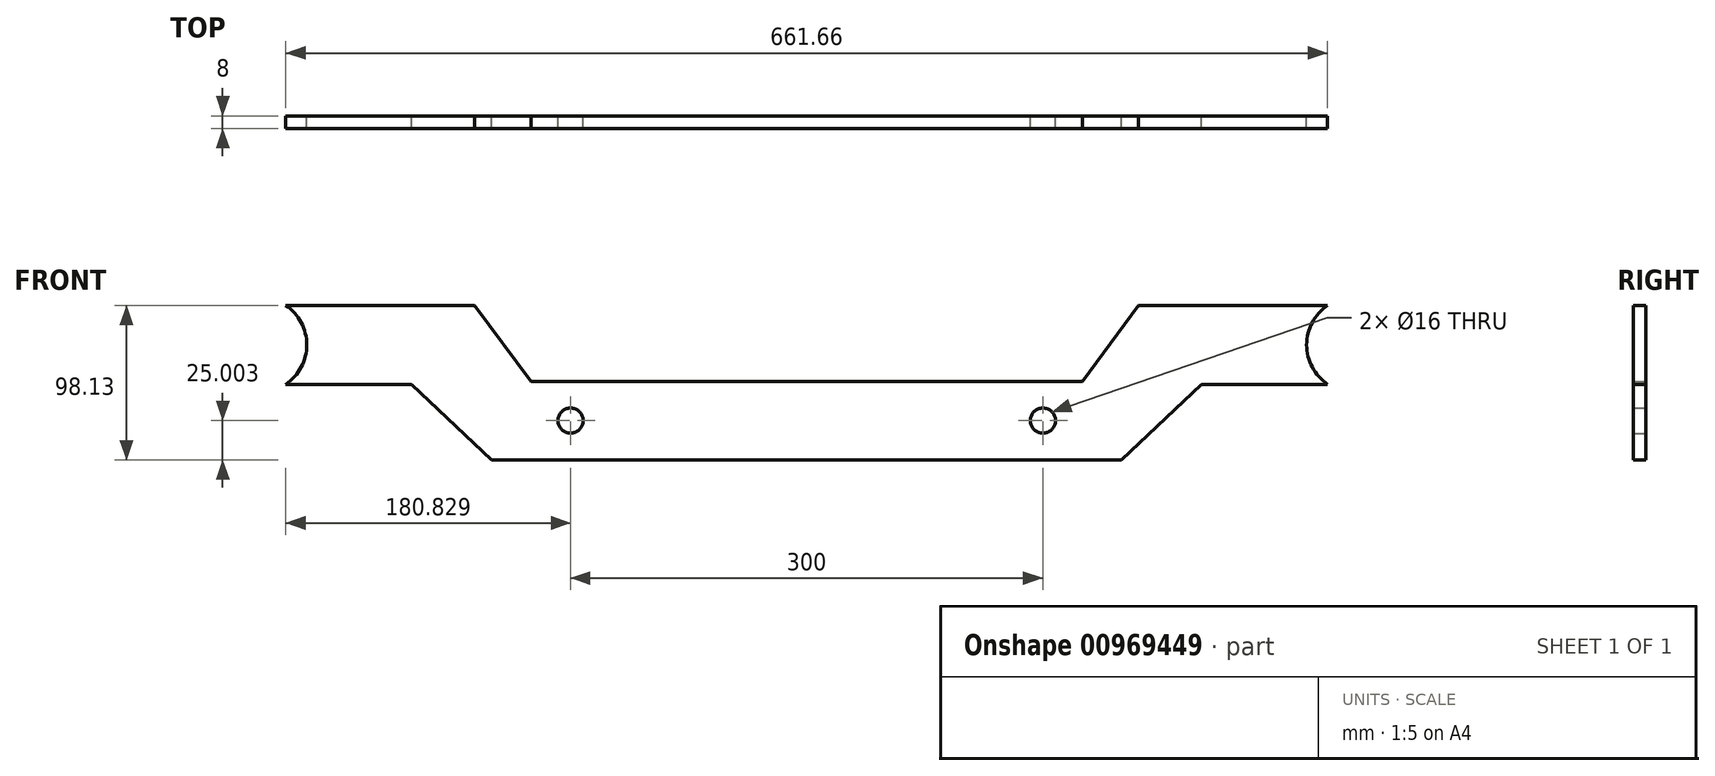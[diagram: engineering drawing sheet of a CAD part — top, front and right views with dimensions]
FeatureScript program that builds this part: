
annotation { "Feature Type Name" : "Feature", "Feature Type Description" : "" }
export const myFeature = defineFeature(function(context is Context, id is Id, definition is map)
    precondition{}
    {
        {
            var Q0;
            Q0=qCreatedBy(makeId("Front.planeOp"),FACE);
            var sketch = newSketch(context, id + "F0", { "sketchPlane" : qUnion([Q0])});
            skLineSegment(sketch, "E0", {"start": v(-200.2, -56.86) * mm, "end": v(199.8, -56.86) * mm});
            skLineSegment(sketch, "E1", {"start": v(-200.2, -56.86) * mm, "end": v(-251.02, -8.73) * mm});
            skLineSegment(sketch, "E2", {"start": v(-251.02, -8.73) * mm, "end": v(-331.02, -8.73) * mm});
            skLineSegment(sketch, "E3", {"start": v(-331.02, 41.27) * mm, "end": v(-211.02, 41.27) * mm});
            skLineSegment(sketch, "E4", {"start": v(-211.02, 41.27) * mm, "end": v(-175.2, -6.86) * mm});
            skLineSegment(sketch, "E5", {"start": v(-175.2, -6.86) * mm, "end": v(174.8, -6.86) * mm});
            skLineSegment(sketch, "E6", {"start": v(-0.2, -56.86) * mm, "end": v(-0.2, 65.39) * mm, "construction": true});
            skCircle(sketch, "E7", {"center": v(-347.88, 16.27) * mm, "radius": 30.15 * mm});
            skLineSegment(sketch, "E8.MirrorCS", {"start": v(210.64, 41.27) * mm, "end": v(174.8, -6.86) * mm});
            skLineSegment(sketch, "E9.MirrorCS", {"start": v(199.8, -56.86) * mm, "end": v(250.64, -8.73) * mm});
            skLineSegment(sketch, "E10.MirrorCS", {"start": v(250.64, -8.73) * mm, "end": v(330.64, -8.73) * mm});
            skLineSegment(sketch, "E11.MirrorCS", {"start": v(330.64, 41.27) * mm, "end": v(210.64, 41.27) * mm});
            skCircle(sketch, "E12.MirrorC", {"center": v(347.5, 16.27) * mm, "radius": 30.15 * mm});
            skCircle(sketch, "E13", {"center": v(-150.2, -31.86) * mm, "radius": 8 * mm});
            skCircle(sketch, "E14.MirrorC", {"center": v(149.8, -31.86) * mm, "radius": 8 * mm});
            skSolve(sketch);
        }
        {
            var Q0;
            Q0=makeQuery(id+"F0.imprint","IMPRINT",FACE,{"disambiguationData":[TD([[makeQuery(id+"F0.imprint","IMPRINT",EDGE,{"derivedFrom":sQuery(id+"F0.wireOp",EDGE,"E0")}),1.0]])]});
            extrude(context, id + "F1", {"entities" : qUnion([Q0]), "depth" : 8 * mm, "offsetDistance" : 25 * mm});
        }
    });
